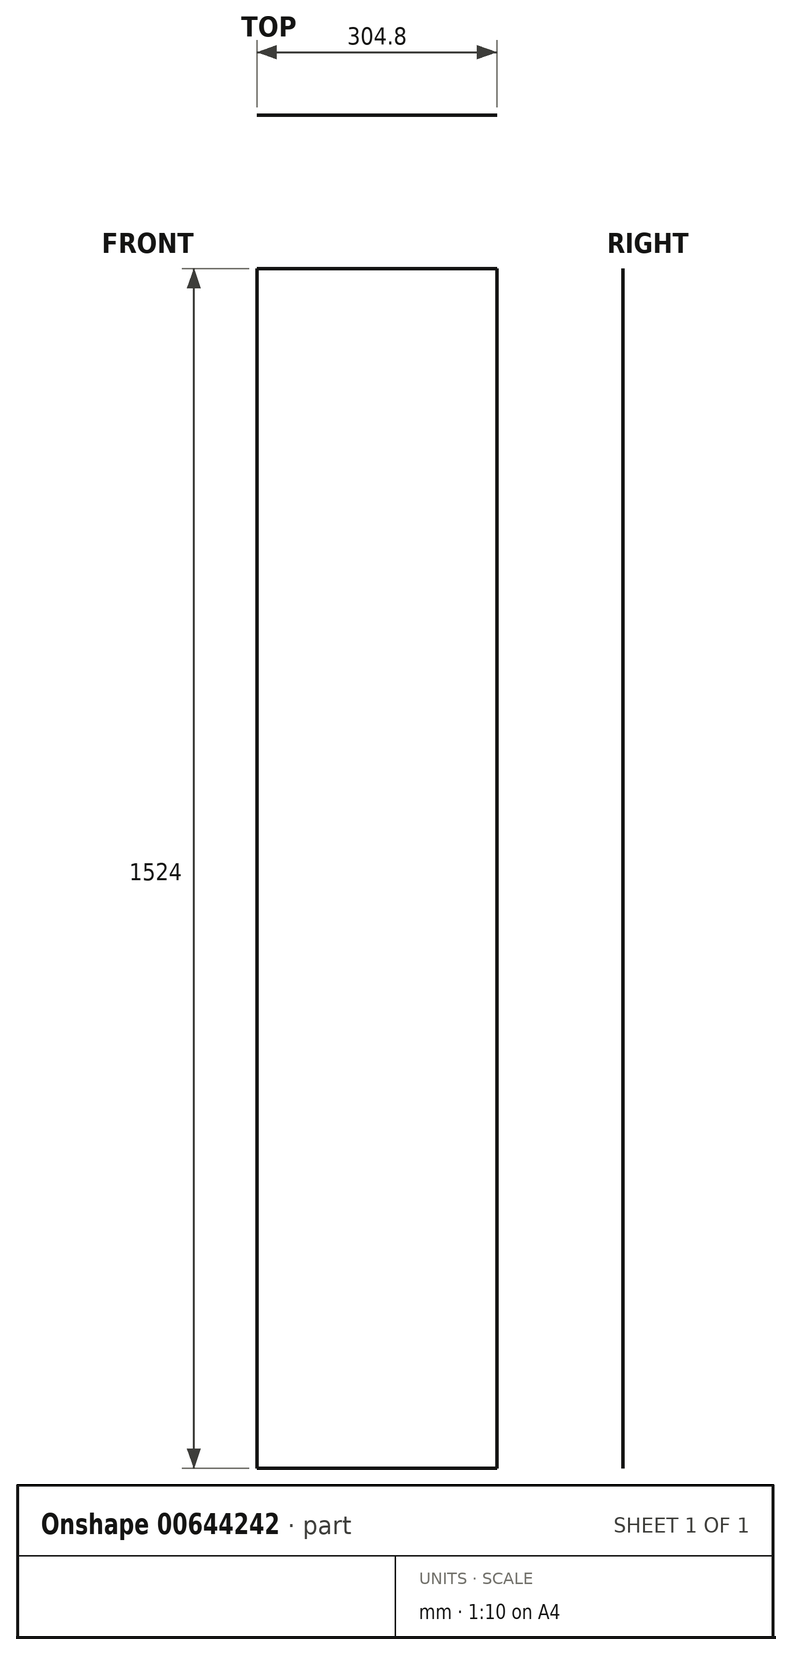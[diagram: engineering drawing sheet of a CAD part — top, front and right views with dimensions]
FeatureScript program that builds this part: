
annotation { "Feature Type Name" : "Feature", "Feature Type Description" : "" }
export const myFeature = defineFeature(function(context is Context, id is Id, definition is map)
    precondition{}
    {
        {
            var Q0;
            Q0=qCreatedBy(makeId("Front.planeOp"),FACE);
            var sketch = newSketch(context, id + "F0", { "sketchPlane" : qUnion([Q0])});
            skLineSegment(sketch, "E0.bottom", {"start": v(0, 0) * mm, "end": v(304.8, 0) * mm});
            skLineSegment(sketch, "E0.top", {"start": v(0, 1524) * mm, "end": v(304.8, 1524) * mm});
            skLineSegment(sketch, "E0.left", {"start": v(0, 0) * mm, "end": v(0, 1524) * mm});
            skLineSegment(sketch, "E0.right", {"start": v(304.8, 0) * mm, "end": v(304.8, 1524) * mm});
            skSolve(sketch);
        }
        {
            var Q0;
            Q0=qSketchRegion(id+"F0",true);
            extrude(context, id + "F1", {"entities" : qUnion([Q0]), "depth" : 1 / 203.2 * mm, "offsetDistance" : 25.4 * mm});
        }
    });
